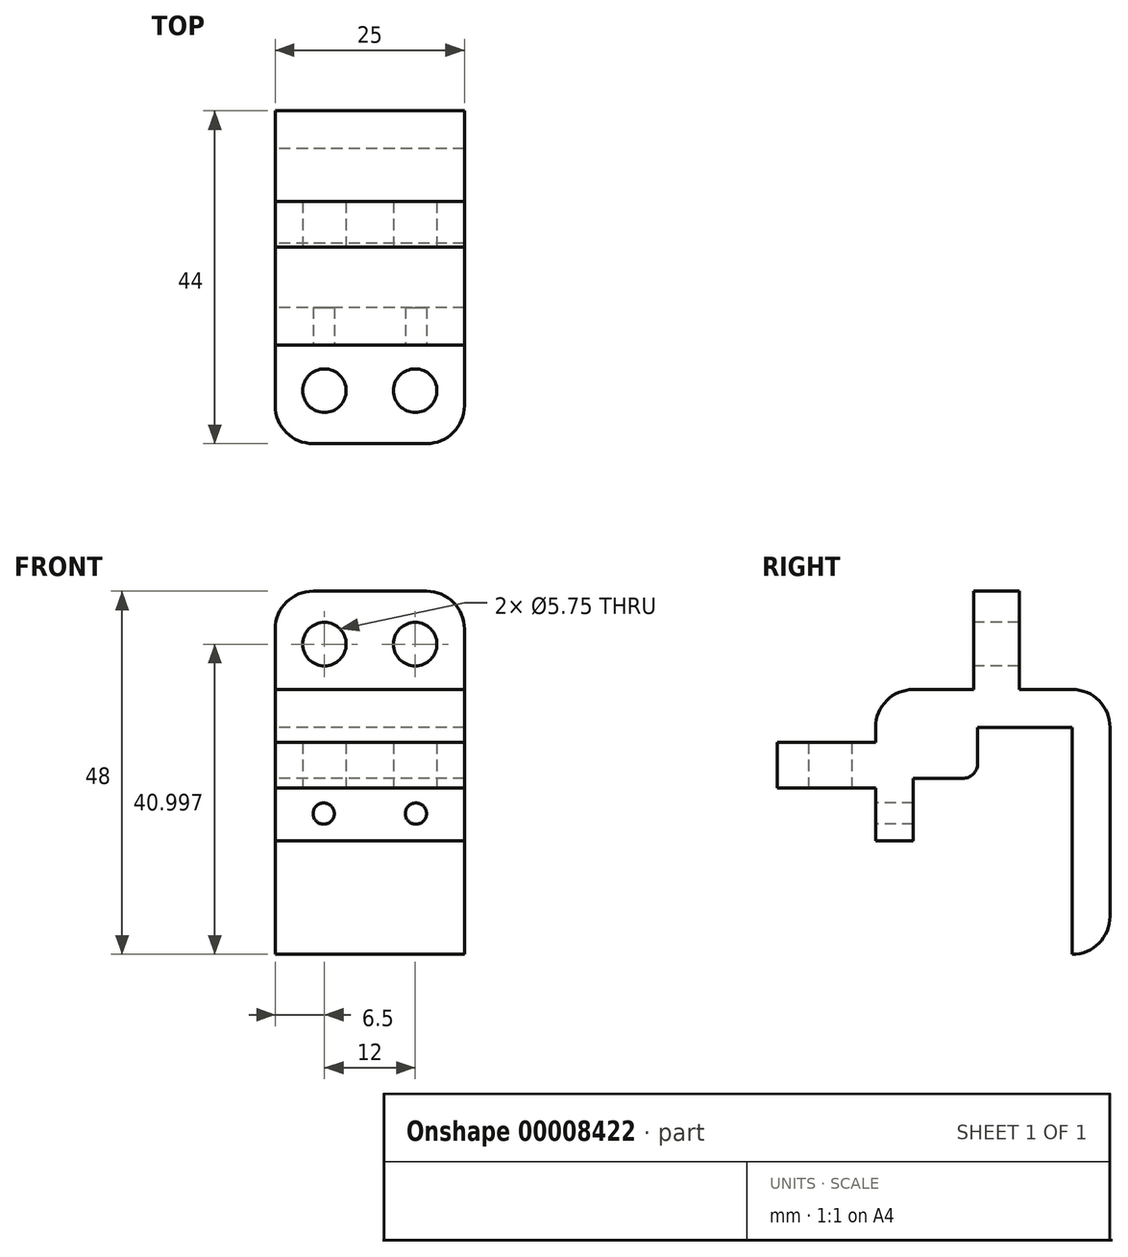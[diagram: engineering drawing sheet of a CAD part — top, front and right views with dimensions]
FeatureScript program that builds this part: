
annotation { "Feature Type Name" : "Feature", "Feature Type Description" : "" }
export const myFeature = defineFeature(function(context is Context, id is Id, definition is map)
    precondition{}
    {
        {
            var Q0;
            Q0=qCreatedBy(makeId("Right.planeOp"),FACE);
            var sketch = newSketch(context, id + "F0", { "sketchPlane" : qUnion([Q0])});
            skLineSegment(sketch, "E0", {"start": v(10.72, 36.3) * mm, "end": v(10.72, 6.3) * mm});
            skLineSegment(sketch, "E1", {"start": v(10.72, 36.3) * mm, "end": v(-10.28, 36.3) * mm});
            skLineSegment(sketch, "E2", {"start": v(-10.28, 36.3) * mm, "end": v(-10.28, 21.3) * mm});
            skLineSegment(sketch, "E3", {"start": v(-10.28, 21.3) * mm, "end": v(-15.28, 21.3) * mm});
            skLineSegment(sketch, "E4", {"start": v(-15.28, 21.3) * mm, "end": v(-15.28, 41.3) * mm});
            skLineSegment(sketch, "E5", {"start": v(-15.28, 41.3) * mm, "end": v(15.72, 41.3) * mm});
            skLineSegment(sketch, "E6", {"start": v(15.72, 41.3) * mm, "end": v(15.72, 6.3) * mm});
            skLineSegment(sketch, "E7", {"start": v(15.72, 6.3) * mm, "end": v(10.72, 6.3) * mm});
            skLineSegment(sketch, "E8", {"start": v(-10.28, 29.56) * mm, "end": v(-1.78, 29.56) * mm});
            skLineSegment(sketch, "E9", {"start": v(-1.78, 29.56) * mm, "end": v(-1.78, 36.3) * mm});
            skSolve(sketch);
        }
        {
            var Q0;
            Q0=qSketchRegion(id+"F0",true);
            extrude(context, id + "F1", {"entities" : qUnion([Q0]), "depth" : 25 * mm});
        }
        {
            var Q0;
            Q0=makeQuery(id+"F1.opExtrude","SWEPT_FACE",FACE,{"disambiguationData":[OSD([sQuery(id+"F0.wireOp",EDGE,"E4")])]});
            var sketch = newSketch(context, id + "F2", { "sketchPlane" : qUnion([Q0])});
            skCircle(sketch, "E10", {"center": v(6.4, 24.9) * mm, "radius": 1.4 * mm});
            skCircle(sketch, "E11", {"center": v(18.6, 24.9) * mm, "radius": 1.4 * mm});
            skLineSegment(sketch, "E12", {"start": v(0, 34.3) * mm, "end": v(25, 34.3) * mm});
            skLineSegment(sketch, "E13", {"start": v(0, 28.3) * mm, "end": v(25, 28.3) * mm});
            skSolve(sketch);
        }
        {
            var Q0;
            {var subQ3=sQuery(id+"F2.wireOp",EDGE,"E12");Q0=makeQuery(id+"F2.imprint","IMPRINT",FACE,{"disambiguationData":[TD([[makeQuery(id+"F2.imprint","IMPRINT",EDGE,{"derivedFrom":subQ3}),-1.0]])]});}
            extrude(context, id + "F3", {"entities" : qUnion([Q0]), "operationType" : NewBodyOperationType.ADD, "depth" : 13 * mm});
        }
        {
            var Q0;
            Q0 = qSketchRegion(id + "F2", true);
            extrude(context, id + "F4", {"entities" : qUnion([Q0]), "operationType" : NewBodyOperationType.REMOVE, "oppositeDirection" : true, "depth" : 5 * mm});
        }
        {
            var Q0;
            Q0=makeQuery(id+"F3.opExtrude","SWEPT_FACE",FACE,{"disambiguationData":[OSD([sQuery(id+"F2.wireOp",EDGE,"E13")])]});
            var sketch = newSketch(context, id + "F5", { "sketchPlane" : qUnion([Q0])});
            skCircle(sketch, "E14", {"center": v(6.5, 21.28) * mm, "radius": 2.88 * mm});
            skCircle(sketch, "E15", {"center": v(18.5, 21.28) * mm, "radius": 2.88 * mm});
            skSolve(sketch);
        }
        {
            var Q0;
            Q0=makeQuery(id+"F5.imprint","IMPRINT",FACE,{"disambiguationData":[TD([[makeQuery(id+"F5.imprint","IMPRINT",EDGE,{"derivedFrom":sQuery(id+"F5.wireOp",EDGE,"E14")}),1.0]])]});
            var Q1;
            Q1=makeQuery(id+"F5.imprint","IMPRINT",FACE,{"disambiguationData":[TD([[makeQuery(id+"F5.imprint","IMPRINT",EDGE,{"derivedFrom":sQuery(id+"F5.wireOp",EDGE,"E15")}),1.0]])]});
            extrude(context, id + "F6", {"entities" : qUnion([Q0, Q1]), "operationType" : NewBodyOperationType.REMOVE, "oppositeDirection" : true, "depth" : 8 * mm});
        }
        {
            var Q0;
            Q0=makeQuery(id+"F1.opExtrude","SWEPT_FACE",FACE,{"disambiguationData":[OSD([sQuery(id+"F0.wireOp",EDGE,"E5")])]});
            var sketch = newSketch(context, id + "F7", { "sketchPlane" : qUnion([Q0])});
            skLineSegment(sketch, "E16", {"start": v(0, -2.28) * mm, "end": v(25, -2.28) * mm});
            skLineSegment(sketch, "E17", {"start": v(0, 3.72) * mm, "end": v(25, 3.72) * mm});
            skSolve(sketch);
        }
        {
            var Q0;
            {var subQ3=sQuery(id+"F7.wireOp",EDGE,"E16");Q0=makeQuery(id+"F7.imprint","IMPRINT",FACE,{"disambiguationData":[TD([[makeQuery(id+"F7.imprint","IMPRINT",EDGE,{"derivedFrom":subQ3}),1.0]])]});}
            extrude(context, id + "F8", {"entities" : qUnion([Q0]), "operationType" : NewBodyOperationType.ADD, "depth" : 13 * mm});
        }
        {
            var Q0;
            Q0=makeQuery(id+"F8.opExtrude","SWEPT_FACE",FACE,{"disambiguationData":[OSD([sQuery(id+"F7.wireOp",EDGE,"E16")])]});
            var sketch = newSketch(context, id + "F9", { "sketchPlane" : qUnion([Q0])});
            skCircle(sketch, "E18", {"center": v(6.5, 47.3) * mm, "radius": 2.88 * mm});
            skCircle(sketch, "E19", {"center": v(18.5, 47.3) * mm, "radius": 2.88 * mm});
            skSolve(sketch);
        }
        {
            var Q0;
            Q0 = qSketchRegion(id + "F9", true);
            extrude(context, id + "F10", {"entities" : qUnion([Q0]), "operationType" : NewBodyOperationType.REMOVE, "oppositeDirection" : true, "depth" : 6 * mm});
        }
        {
            var Q0;
            Q0=makeQuery(id+"F1.opExtrude","SWEPT_EDGE",EDGE,{"disambiguationData":[OSD([sQuery(id+"F0.wireOp",EDGE,"E4"),sQuery(id+"F0.wireOp",EDGE,"E5")])]});
            var Q1;
            {var subQ0=sQuery(id+"F0.wireOp",EDGE,"E4");var subQ1=makeQuery(id+"F1.opExtrude","CAP_EDGE",EDGE,{"disambiguationData":[OSD([subQ0])],"isStart":true});Q1=makeQuery(id+"F3.opExtrude","CAP_EDGE",EDGE,{"disambiguationData":[OSD([subQ0]),TDD([makeQuery(id+"F2.imprint","IMPRINT",EDGE,{"disambiguationData":[TD([[makeQuery(id+"F2.imprint","INTERSECT",VERTEX,{"derivedFrom":[subQ1,sQuery(id+"F2.wireOp",EDGE,"E12")]}),1.0]])],"derivedFrom":subQ1})])],"isStart":false});}
            var Q2;
            {var subQ0=sQuery(id+"F0.wireOp",EDGE,"E4");var subQ1=makeQuery(id+"F1.opExtrude","CAP_EDGE",EDGE,{"disambiguationData":[OSD([subQ0])],"isStart":false});Q2=makeQuery(id+"F3.opExtrude","CAP_EDGE",EDGE,{"disambiguationData":[OSD([subQ0]),TDD([makeQuery(id+"F2.imprint","IMPRINT",EDGE,{"disambiguationData":[TD([[makeQuery(id+"F2.imprint","INTERSECT",VERTEX,{"derivedFrom":[subQ1,sQuery(id+"F2.wireOp",EDGE,"E12")]}),1.0]])],"derivedFrom":subQ1})])],"isStart":false});}
            var Q3;
            {var subQ0=sQuery(id+"F0.wireOp",EDGE,"E5");var subQ1=makeQuery(id+"F1.opExtrude","CAP_EDGE",EDGE,{"disambiguationData":[OSD([subQ0])],"isStart":true});Q3=makeQuery(id+"F8.opExtrude","CAP_EDGE",EDGE,{"disambiguationData":[OSD([subQ0]),TDD([makeQuery(id+"F7.imprint","IMPRINT",EDGE,{"disambiguationData":[TD([[makeQuery(id+"F7.imprint","INTERSECT",VERTEX,{"derivedFrom":[subQ1,sQuery(id+"F7.wireOp",EDGE,"E16")]}),-1.0]])],"derivedFrom":subQ1})])],"isStart":false});}
            var Q4;
            {var subQ0=sQuery(id+"F0.wireOp",EDGE,"E5");var subQ1=makeQuery(id+"F1.opExtrude","CAP_EDGE",EDGE,{"disambiguationData":[OSD([subQ0])],"isStart":false});Q4=makeQuery(id+"F8.opExtrude","CAP_EDGE",EDGE,{"disambiguationData":[OSD([subQ0]),TDD([makeQuery(id+"F7.imprint","IMPRINT",EDGE,{"disambiguationData":[TD([[makeQuery(id+"F7.imprint","INTERSECT",VERTEX,{"derivedFrom":[subQ1,sQuery(id+"F7.wireOp",EDGE,"E16")]}),-1.0]])],"derivedFrom":subQ1})])],"isStart":false});}
            var Q5;
            Q5=makeQuery(id+"F1.opExtrude","SWEPT_EDGE",EDGE,{"disambiguationData":[OSD([sQuery(id+"F0.wireOp",EDGE,"E5"),sQuery(id+"F0.wireOp",EDGE,"E6")])]});
            var Q6;
            Q6=makeQuery(id+"F1.opExtrude","SWEPT_EDGE",EDGE,{"disambiguationData":[OSD([sQuery(id+"F0.wireOp",EDGE,"E6"),sQuery(id+"F0.wireOp",EDGE,"E7")])]});
            fillet(context, id + "F11", {"entities" : qUnion([Q0, Q1, Q2, Q3, Q4, Q5, Q6]), "radius" : 5 * mm, "tangentPropagation" : true, "allowEdgeOverflow" : false});
        }
        {
            var Q0;
            Q0=makeQuery(id+"F1.opExtrude","SWEPT_EDGE",EDGE,{"disambiguationData":[OSD([sQuery(id+"F0.wireOp",EDGE,"E8"),sQuery(id+"F0.wireOp",EDGE,"E9")])]});
            fillet(context, id + "F12", {"entities" : qUnion([Q0]), "radius" : 2 * mm, "tangentPropagation" : true, "allowEdgeOverflow" : false});
        }
    });
